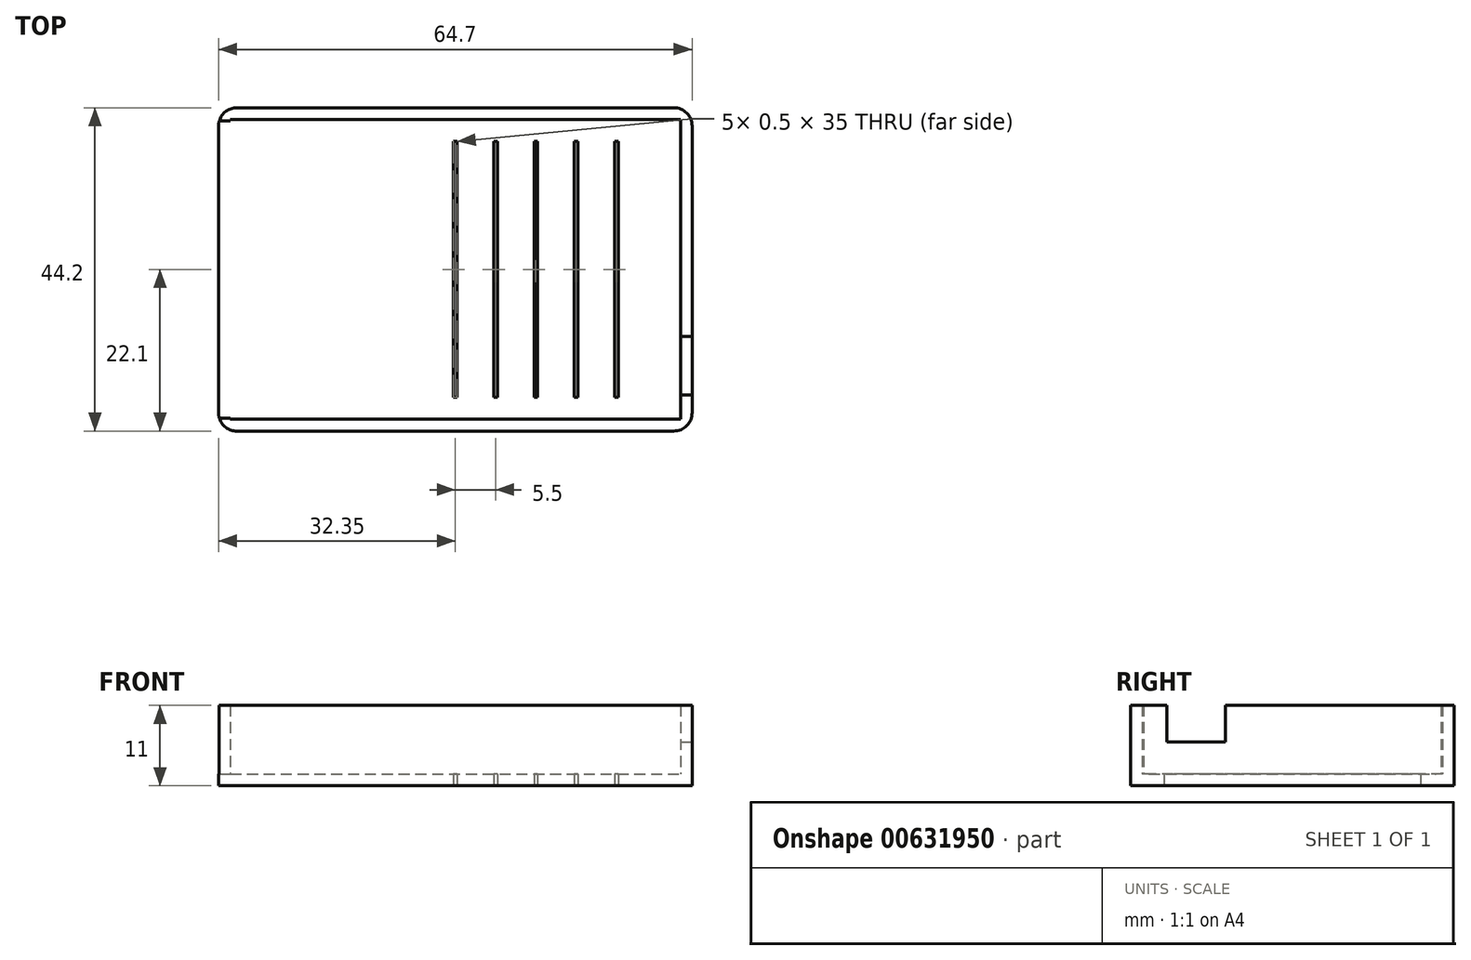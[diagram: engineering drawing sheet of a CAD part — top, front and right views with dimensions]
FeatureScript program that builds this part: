
annotation { "Feature Type Name" : "Feature", "Feature Type Description" : "" }
export const myFeature = defineFeature(function(context is Context, id is Id, definition is map)
    precondition{}
    {
        {
            var Q0;
            Q0=qCreatedBy(makeId("Top.planeOp"),FACE);
            var sketch = newSketch(context, id + "F0", { "sketchPlane" : qUnion([Q0])});
            skLineSegment(sketch, "E0.bottom", {"start": v(30.25, -20.32) * mm, "end": v(-30.25, -20.32) * mm});
            skLineSegment(sketch, "E0.top", {"start": v(30.25, 20.32) * mm, "end": v(-30.25, 20.32) * mm});
            skLineSegment(sketch, "E0.left", {"start": v(30.25, -20.32) * mm, "end": v(30.25, 20.32) * mm});
            skLineSegment(sketch, "E0.right", {"start": v(-30.25, -20.32) * mm, "end": v(-30.25, 20.32) * mm});
            skPoint(sketch, "E0.middle", {"position": v(0, 0) * mm});
            skSolve(sketch);
        }
        {
            var Q0;
            Q0=makeQuery(id+"F0.imprint","IMPRINT",FACE,{"disambiguationData":[TD([[makeQuery(id+"F0.imprint","IMPRINT",EDGE,{"derivedFrom":sQuery(id+"F0.wireOp",EDGE,"E0.bottom")}),-1.0]])]});
            extrude(context, id + "F1", {"entities" : qUnion([Q0]), "depth" : 12.7 * mm, "offsetDistance" : 25 * mm});
        }
        {
            var Q0;
            Q0=qCreatedBy(makeId("Top.planeOp"),FACE);
            var sketch = newSketch(context, id + "F2", { "sketchPlane" : qUnion([Q0])});
            skLineSegment(sketch, "E1.bottom", {"start": v(-30.75, 20.5) * mm, "end": v(30.75, 20.5) * mm});
            skLineSegment(sketch, "E1.top", {"start": v(-30.75, -20.5) * mm, "end": v(30.75, -20.5) * mm});
            skLineSegment(sketch, "E1.left", {"start": v(-30.75, 20.5) * mm, "end": v(-30.75, -20.5) * mm});
            skLineSegment(sketch, "E1.right", {"start": v(30.75, 20.5) * mm, "end": v(30.75, -20.5) * mm});
            skPoint(sketch, "E1.middle", {"position": v(0, 0) * mm});
            skLineSegment(sketch, "E2.0", {"start": v(-32.35, 22.1) * mm, "end": v(-32.35, -22.1) * mm});
            skLineSegment(sketch, "E2.1", {"start": v(-32.35, 22.1) * mm, "end": v(32.35, 22.1) * mm});
            skLineSegment(sketch, "E2.2", {"start": v(32.35, 22.1) * mm, "end": v(32.35, -22.1) * mm});
            skLineSegment(sketch, "E2.3", {"start": v(-32.35, -22.1) * mm, "end": v(32.35, -22.1) * mm});
            skSolve(sketch);
        }
        {
            var Q0;
            Q0=makeQuery(id+"F2.imprint","IMPRINT",FACE,{"disambiguationData":[TD([[makeQuery(id+"F2.imprint","IMPRINT",EDGE,{"derivedFrom":sQuery(id+"F2.wireOp",EDGE,"E1.bottom")}),1.0]])]});
            extrude(context, id + "F3", {"entities" : qUnion([Q0]), "depth" : 11 * mm, "offsetDistance" : 25 * mm});
        }
        {
            var Q0;
            Q0=makeQuery(id+"F2.imprint","IMPRINT",FACE,{"disambiguationData":[TD([[makeQuery(id+"F2.imprint","IMPRINT",EDGE,{"derivedFrom":sQuery(id+"F2.wireOp",EDGE,"E1.bottom")}),-1.0]])]});
            extrude(context, id + "F4", {"entities" : qUnion([Q0]), "operationType" : NewBodyOperationType.ADD, "depth" : 1.6 * mm, "offsetDistance" : 25 * mm});
        }
        {
            var Q0;
            Q0=makeQuery(id+"F1.opExtrude","SWEPT_FACE",FACE,{"disambiguationData":[OSD([sQuery(id+"F0.wireOp",EDGE,"E0.right")])]});
            extrude(context, id + "F5", {"entities" : qUnion([Q0]), "operationType" : NewBodyOperationType.REMOVE, "depth" : 8.8 * mm, "offsetDistance" : 25 * mm});
        }
        {
            var Q0;
            {var subQ0=sQuery(id+"F2.wireOp",EDGE,"E1.right");var subQ1=sQuery(id+"F2.wireOp",EDGE,"E1.left");var subQ2=sQuery(id+"F2.wireOp",EDGE,"E1.top");var subQ3=sQuery(id+"F2.wireOp",EDGE,"E1.bottom");Q0=makeQuery(id+"F4.boolean.opBoolean","MERGE",FACE,{"derivedFrom":[makeQuery(id+"F1.opExtrude","CAP_FACE",FACE,{"disambiguationData":[OSD([sQuery(id+"F0.wireOp",EDGE,"E0.bottom"),sQuery(id+"F0.wireOp",EDGE,"E0.top"),sQuery(id+"F0.wireOp",EDGE,"E0.left"),sQuery(id+"F0.wireOp",EDGE,"E0.right")])],"isStart":true}),makeQuery(id+"F3.opExtrude","CAP_FACE",FACE,{"disambiguationData":[OSD([subQ3,subQ2,subQ1,subQ0,sQuery(id+"F2.wireOp",EDGE,"E2.0"),sQuery(id+"F2.wireOp",EDGE,"E2.1"),sQuery(id+"F2.wireOp",EDGE,"E2.2"),sQuery(id+"F2.wireOp",EDGE,"E2.3")])],"isStart":true}),makeQuery(id+"F4.opExtrude","CAP_FACE",FACE,{"disambiguationData":[OSD([subQ3,subQ2,subQ1,subQ0])],"isStart":true})]});}
            var sketch = newSketch(context, id + "F6", { "sketchPlane" : qUnion([Q0])});
            skLineSegment(sketch, "E3.bottom", {"start": v(0.25, -17.5) * mm, "end": v(-0.25, -17.5) * mm});
            skLineSegment(sketch, "E3.top", {"start": v(0.25, 17.5) * mm, "end": v(-0.25, 17.5) * mm});
            skLineSegment(sketch, "E3.left", {"start": v(0.25, -17.5) * mm, "end": v(0.25, 17.5) * mm});
            skLineSegment(sketch, "E3.right", {"start": v(-0.25, -17.5) * mm, "end": v(-0.25, 17.5) * mm});
            skPoint(sketch, "E3.middle", {"position": v(0, 0) * mm});
            skLineSegment(sketch, "E4.1.0.0", {"start": v(5.25, -17.5) * mm, "end": v(5.25, 17.5) * mm});
            skLineSegment(sketch, "E4.1.0.1", {"start": v(5.75, -17.5) * mm, "end": v(5.75, 17.5) * mm});
            skLineSegment(sketch, "E4.1.0.2", {"start": v(5.75, 17.5) * mm, "end": v(5.25, 17.5) * mm});
            skLineSegment(sketch, "E4.1.0.3", {"start": v(5.75, -17.5) * mm, "end": v(5.25, -17.5) * mm});
            skLineSegment(sketch, "E4.2.0.0", {"start": v(10.75, -17.5) * mm, "end": v(10.75, 17.5) * mm});
            skLineSegment(sketch, "E4.2.0.1", {"start": v(11.25, -17.5) * mm, "end": v(11.25, 17.5) * mm});
            skLineSegment(sketch, "E4.2.0.2", {"start": v(11.25, 17.5) * mm, "end": v(10.75, 17.5) * mm});
            skLineSegment(sketch, "E4.2.0.3", {"start": v(11.25, -17.5) * mm, "end": v(10.75, -17.5) * mm});
            skLineSegment(sketch, "E4.3.0.0", {"start": v(16.25, -17.5) * mm, "end": v(16.25, 17.5) * mm});
            skLineSegment(sketch, "E4.3.0.1", {"start": v(16.75, -17.5) * mm, "end": v(16.75, 17.5) * mm});
            skLineSegment(sketch, "E4.3.0.2", {"start": v(16.75, 17.5) * mm, "end": v(16.25, 17.5) * mm});
            skLineSegment(sketch, "E4.3.0.3", {"start": v(16.75, -17.5) * mm, "end": v(16.25, -17.5) * mm});
            skLineSegment(sketch, "E4.4.0.0", {"start": v(21.75, -17.5) * mm, "end": v(21.75, 17.5) * mm});
            skLineSegment(sketch, "E4.4.0.1", {"start": v(22.25, -17.5) * mm, "end": v(22.25, 17.5) * mm});
            skLineSegment(sketch, "E4.4.0.2", {"start": v(22.25, 17.5) * mm, "end": v(21.75, 17.5) * mm});
            skLineSegment(sketch, "E4.4.0.3", {"start": v(22.25, -17.5) * mm, "end": v(21.75, -17.5) * mm});
            skLineSegment(sketch, "E4.direction1", {"start": v(-1.25, -17.5) * mm, "end": v(4.25, -17.5) * mm, "construction": true});
            skSolve(sketch);
        }
        {
            var Q0;
            Q0=makeQuery(id+"F6.imprint","IMPRINT",FACE,{"disambiguationData":[TD([[makeQuery(id+"F6.imprint","IMPRINT",EDGE,{"derivedFrom":sQuery(id+"F6.wireOp",EDGE,"8e398a63-83e2-4040-b939-5b825b0c38a3.1.0.0")}),1.0]])]});
            var Q1;
            Q1=makeQuery(id+"F6.imprint","IMPRINT",FACE,{"disambiguationData":[TD([[makeQuery(id+"F6.imprint","IMPRINT",EDGE,{"derivedFrom":sQuery(id+"F6.wireOp",EDGE,"8e398a63-83e2-4040-b939-5b825b0c38a3.1.1.0")}),1.0]])]});
            var Q2;
            {var subQ0=sQuery(id+"F6.wireOp",EDGE,"3RJRcBtm-TKJ7-8kVH-7u0y-wL5ELAvEqava.left");Q2=makeQuery(id+"F6.imprint","IMPRINT",FACE,{"disambiguationData":[TD([[makeQuery(id+"F6.imprint","IMPRINT",EDGE,{"derivedFrom":subQ0}),1.0]])]});}
            var Q3;
            {var subQ0=sQuery(id+"F6.wireOp",EDGE,"0e4ed41f-c656-4a6a-a3c6-04501d88f38e.0.1.2");Q3=makeQuery(id+"F6.imprint","IMPRINT",FACE,{"disambiguationData":[TD([[makeQuery(id+"F6.imprint","IMPRINT",EDGE,{"derivedFrom":subQ0}),1.0]])]});}
            var Q4;
            {var subQ0=sQuery(id+"F6.wireOp",EDGE,"0e4ed41f-c656-4a6a-a3c6-04501d88f38e.0.2.2");Q4=makeQuery(id+"F6.imprint","IMPRINT",FACE,{"disambiguationData":[TD([[makeQuery(id+"F6.imprint","IMPRINT",EDGE,{"derivedFrom":subQ0}),1.0]])]});}
            var Q5;
            {var subQ0=sQuery(id+"F6.wireOp",EDGE,"0e4ed41f-c656-4a6a-a3c6-04501d88f38e.0.3.2");Q5=makeQuery(id+"F6.imprint","IMPRINT",FACE,{"disambiguationData":[TD([[makeQuery(id+"F6.imprint","IMPRINT",EDGE,{"derivedFrom":subQ0}),1.0]])]});}
            var Q6;
            Q6=makeQuery(id+"F6.imprint","IMPRINT",FACE,{"disambiguationData":[TD([[makeQuery(id+"F6.imprint","IMPRINT",EDGE,{"derivedFrom":sQuery(id+"F6.wireOp",EDGE,"E4.4.0.0")}),-1.0]])]});
            var Q7;
            Q7=makeQuery(id+"F6.imprint","IMPRINT",FACE,{"disambiguationData":[TD([[makeQuery(id+"F6.imprint","IMPRINT",EDGE,{"derivedFrom":sQuery(id+"F6.wireOp",EDGE,"E4.3.0.0")}),-1.0]])]});
            var Q8;
            Q8=makeQuery(id+"F6.imprint","IMPRINT",FACE,{"disambiguationData":[TD([[makeQuery(id+"F6.imprint","IMPRINT",EDGE,{"derivedFrom":sQuery(id+"F6.wireOp",EDGE,"E4.2.0.0")}),-1.0]])]});
            var Q9;
            Q9=makeQuery(id+"F6.imprint","IMPRINT",FACE,{"disambiguationData":[TD([[makeQuery(id+"F6.imprint","IMPRINT",EDGE,{"derivedFrom":sQuery(id+"F6.wireOp",EDGE,"E4.1.0.0")}),-1.0]])]});
            var Q10;
            Q10=makeQuery(id+"F6.imprint","IMPRINT",FACE,{"disambiguationData":[TD([[makeQuery(id+"F6.imprint","IMPRINT",EDGE,{"derivedFrom":sQuery(id+"F6.wireOp",EDGE,"E3.bottom")}),-1.0]])]});
            extrude(context, id + "F7", {"entities" : qUnion([Q0, Q1, Q2, Q3, Q4, Q5, Q6, Q7, Q8, Q9, Q10]), "operationType" : NewBodyOperationType.REMOVE, "oppositeDirection" : true, "depth" : 16 * mm, "offsetDistance" : 25 * mm});
        }
        {
            var Q0;
            Q0=makeQuery(id+"F1.opExtrude","SWEPT_FACE",FACE,{"disambiguationData":[OSD([sQuery(id+"F0.wireOp",EDGE,"E0.right")])]});
            extrude(context, id + "F8", {"entities" : qUnion([Q0]), "operationType" : NewBodyOperationType.REMOVE, "oppositeDirection" : true, "depth" : 60.7 * mm, "offsetDistance" : 25 * mm});
        }
        {
            var Q0;
            Q0=makeQuery(id+"F3.opExtrude","SWEPT_EDGE",EDGE,{"disambiguationData":[OSD([sQuery(id+"F2.wireOp",EDGE,"E2.1"),sQuery(id+"F2.wireOp",EDGE,"E2.2")])]});
            var Q1;
            Q1=makeQuery(id+"F3.opExtrude","SWEPT_EDGE",EDGE,{"disambiguationData":[OSD([sQuery(id+"F2.wireOp",EDGE,"E2.2"),sQuery(id+"F2.wireOp",EDGE,"E2.3")])]});
            fillet(context, id + "F9", {"entities" : qUnion([Q0, Q1]), "radius" : 2.5 * mm, "tangentPropagation" : true, "allowEdgeOverflow" : false});
        }
        {
            var Q0;
            Q0=makeQuery(id+"F3.opExtrude","SWEPT_EDGE",EDGE,{"disambiguationData":[OSD([sQuery(id+"F2.wireOp",EDGE,"E2.0"),sQuery(id+"F2.wireOp",EDGE,"E2.1")])]});
            var Q1;
            Q1=makeQuery(id+"F3.opExtrude","SWEPT_EDGE",EDGE,{"disambiguationData":[OSD([sQuery(id+"F2.wireOp",EDGE,"E2.0"),sQuery(id+"F2.wireOp",EDGE,"E2.3")])]});
            fillet(context, id + "F10", {"entities" : qUnion([Q0, Q1]), "radius" : 2.5 * mm, "tangentPropagation" : true, "allowEdgeOverflow" : false});
        }
        {
            var Q0;
            Q0=makeQuery(id+"F3.opExtrude","SWEPT_FACE",FACE,{"disambiguationData":[OSD([sQuery(id+"F2.wireOp",EDGE,"E2.2")])]});
            var sketch = newSketch(context, id + "F11", { "sketchPlane" : qUnion([Q0])});
            skLineSegment(sketch, "E5.bottom", {"start": v(17.17, 6) * mm, "end": v(9.17, 6) * mm});
            skLineSegment(sketch, "E5.top", {"start": v(17.17, 11) * mm, "end": v(9.17, 11) * mm});
            skLineSegment(sketch, "E5.left", {"start": v(17.17, 6) * mm, "end": v(17.17, 11) * mm});
            skLineSegment(sketch, "E5.right", {"start": v(9.17, 6) * mm, "end": v(9.17, 11) * mm});
            skSolve(sketch);
        }
        {
            var Q0;
            Q0=makeQuery(id+"F11.imprint","IMPRINT",FACE,{"disambiguationData":[TD([[makeQuery(id+"F11.imprint","IMPRINT",EDGE,{"derivedFrom":sQuery(id+"F11.wireOp",EDGE,"E5.bottom")}),-1.0]])]});
            extrude(context, id + "F12", {"entities" : qUnion([Q0]), "oppositeDirection" : true, "depth" : 1.71 * mm, "offsetDistance" : 25 * mm});
        }
        {
            var Q0;
            Q0=makeQuery(id+"F3.opExtrude","SWEPT_FACE",FACE,{"disambiguationData":[OSD([sQuery(id+"F2.wireOp",EDGE,"E2.1")])]});
            var Q1;
            Q1=makeQuery(id+"F3.opExtrude","SWEPT_FACE",FACE,{"disambiguationData":[OSD([sQuery(id+"F2.wireOp",EDGE,"E2.3")])]});
            cPlane(context, id + "F13", {"entities" : qUnion([Q0, Q1]), "cplaneType" : CPlaneType.MID_PLANE, "offset" : 25 * mm, "width" : 150 * mm, "height" : 150 * mm});
        }
        {
            var Q0;
            Q0=makeQuery(id+"F12.opExtrude","SWEPT_BODY",BODY,{"disambiguationData":[OSD([sQuery(id+"F11.wireOp",EDGE,"E5.bottom"),sQuery(id+"F11.wireOp",EDGE,"E5.top"),sQuery(id+"F11.wireOp",EDGE,"E5.left"),sQuery(id+"F11.wireOp",EDGE,"E5.right")])]});
            var Q1;
            Q1=qCreatedBy(id+"F13.planeOp",FACE);
            mirror(context, id + "F14", {"operationType" : NewBodyOperationType.REMOVE, "entities" : qUnion([Q0]), "mirrorPlane" : qUnion([Q1])});
        }
        {
            var Q0;
            Q0=makeQuery(id+"F12.opExtrude","SWEPT_BODY",BODY,{"disambiguationData":[OSD([sQuery(id+"F11.wireOp",EDGE,"E5.bottom"),sQuery(id+"F11.wireOp",EDGE,"E5.top"),sQuery(id+"F11.wireOp",EDGE,"E5.left"),sQuery(id+"F11.wireOp",EDGE,"E5.right")])]});
            deleteBodies(context, id + "F15", {"entities" : qUnion([Q0])});
        }
    });
